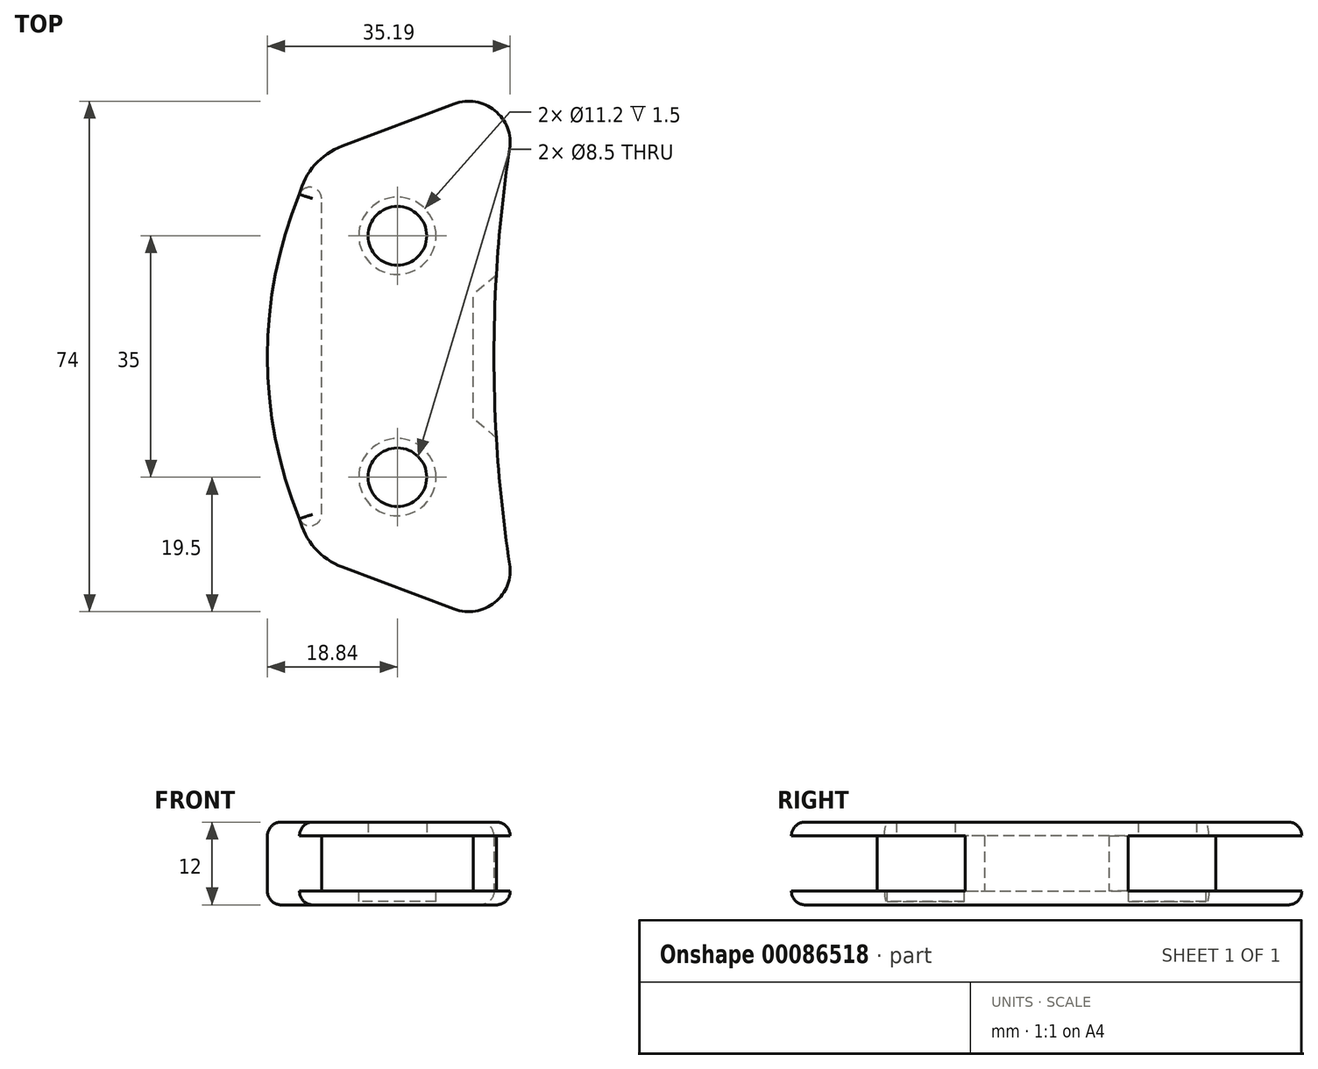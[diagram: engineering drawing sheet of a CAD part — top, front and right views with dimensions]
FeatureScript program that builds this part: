
annotation { "Feature Type Name" : "Feature", "Feature Type Description" : "" }
export const myFeature = defineFeature(function(context is Context, id is Id, definition is map)
    precondition{}
    {
        {
            var Q0;
            Q0=qCreatedBy(makeId("Top.planeOp"),FACE);
            var sketch = newSketch(context, id + "F0", { "sketchPlane" : qUnion([Q0])});
            skCircle(sketch, "E0", {"center": v(0, 17.5) * mm, "radius": 5.6 * mm, "construction": true});
            skCircle(sketch, "E1", {"center": v(0, -17.5) * mm, "radius": 5.6 * mm, "construction": true});
            skLineSegment(sketch, "E2", {"start": v(0, 17.5) * mm, "end": v(0, -17.5) * mm, "construction": true});
            skArc(sketch, "E3", {"start": v(15, 17.5) * mm, "mid": v(0, 32.5) * mm, "end": v(-15, 17.5) * mm, "construction": true});
            skArc(sketch, "E4", {"start": v(-15, -17.5) * mm, "mid": v(0, -32.5) * mm, "end": v(15, -17.5) * mm, "construction": true});
            skLineSegment(sketch, "E5", {"start": v(-15, 17.5) * mm, "end": v(-15, -17.5) * mm, "construction": true});
            skLineSegment(sketch, "E6", {"start": v(15, 17.5) * mm, "end": v(15, -17.5) * mm, "construction": true});
            skArc(sketch, "E7.0", {"start": v(18, 17.5) * mm, "mid": v(0, 35.5) * mm, "end": v(-18, 17.5) * mm, "construction": true});
            skLineSegment(sketch, "E7.1", {"start": v(18, 17.5) * mm, "end": v(18, -17.5) * mm, "construction": true});
            skArc(sketch, "E7.2", {"start": v(-18, -17.5) * mm, "mid": v(0, -35.5) * mm, "end": v(18, -17.5) * mm, "construction": true});
            skLineSegment(sketch, "E7.3", {"start": v(-18, 17.5) * mm, "end": v(-18, -17.5) * mm, "construction": true});
            skLineSegment(sketch, "E8", {"start": v(-8, 30.52) * mm, "end": v(8.24, 36.62) * mm});
            skLineSegment(sketch, "E9", {"start": v(-8, -30.52) * mm, "end": v(8.24, -36.62) * mm});
            skArc(sketch, "E10", {"start": v(-14.2, 23.51) * mm, "mid": v(-17, 0) * mm, "end": v(-14.2, -23.51) * mm});
            skArc(sketch, "E11", {"start": v(16.28, 30.1) * mm, "mid": v(14, 0) * mm, "end": v(16.28, -30.1) * mm});
            skArc(sketch, "E12", {"start": v(8.24, 36.62) * mm, "mid": v(14.12, 35.66) * mm, "end": v(16.28, 30.1) * mm});
            skArc(sketch, "E13", {"start": v(8.24, -36.62) * mm, "mid": v(14.12, -35.66) * mm, "end": v(16.28, -30.1) * mm});
            skLineSegment(sketch, "E14", {"start": v(0, 0) * mm, "end": v(83, 0) * mm, "construction": true});
            skLineSegment(sketch, "E15", {"start": v(10.35, 31) * mm, "end": v(10.35, -31) * mm, "construction": true});
            skPoint(sketch, "E16.visualSharp", {"position": v(-12.79, 28.72) * mm});
            skArc(sketch, "E16.filletArc", {"start": v(-8, 30.52) * mm, "mid": v(-11.97, 27.79) * mm, "end": v(-14.2, 23.51) * mm});
            skPoint(sketch, "E17.visualSharp", {"position": v(-12.79, -28.72) * mm});
            skArc(sketch, "E17.filletArc", {"start": v(-14.2, -23.51) * mm, "mid": v(-11.97, -27.79) * mm, "end": v(-8, -30.52) * mm});
            skSolve(sketch);
        }
        {
            var Q0;
            Q0=makeQuery(id+"F0.imprint","IMPRINT",FACE,{"disambiguationData":[TD([[makeQuery(id+"F0.imprint","IMPRINT",EDGE,{"derivedFrom":sQuery(id+"F0.wireOp",EDGE,"E8")}),-1.0]])]});
            extrude(context, id + "F1", {"entities" : qUnion([Q0]), "depth" : 2 * mm});
        }
        {
            var Q0;
            Q0=makeQuery(id+"F1.opExtrude","CAP_FACE",FACE,{"disambiguationData":[OSD([sQuery(id+"F0.wireOp",EDGE,"E8"),sQuery(id+"F0.wireOp",EDGE,"E9"),sQuery(id+"F0.wireOp",EDGE,"E10"),sQuery(id+"F0.wireOp",EDGE,"E11"),sQuery(id+"F0.wireOp",EDGE,"E12"),sQuery(id+"F0.wireOp",EDGE,"E13"),sQuery(id+"F0.wireOp",EDGE,"E16.filletArc"),sQuery(id+"F0.wireOp",EDGE,"E17.filletArc")])],"isStart":false});
            var sketch = newSketch(context, id + "F2", { "sketchPlane" : qUnion([Q0])});
            skCircle(sketch, "E18", {"center": v(0, 17.5) * mm, "radius": 5.6 * mm});
            skCircle(sketch, "E19", {"center": v(0, -17.5) * mm, "radius": 5.6 * mm});
            skLineSegment(sketch, "E20", {"start": v(0, 17.5) * mm, "end": v(0, -17.5) * mm, "construction": true});
            skArc(sketch, "E21", {"start": v(11, 17.5) * mm, "mid": v(0, 28.5) * mm, "end": v(-11, 17.5) * mm, "construction": true});
            skArc(sketch, "E22", {"start": v(-11, -17.5) * mm, "mid": v(0, -28.5) * mm, "end": v(11, -17.5) * mm, "construction": true});
            skLineSegment(sketch, "E23", {"start": v(-11, 17.5) * mm, "end": v(-11, -17.5) * mm, "construction": true});
            skLineSegment(sketch, "E24", {"start": v(11, 17.5) * mm, "end": v(11, -17.5) * mm, "construction": true});
            skArc(sketch, "E25.0", {"start": v(14, 17.5) * mm, "mid": v(0, 31.5) * mm, "end": v(-14, 17.5) * mm, "construction": true});
            skLineSegment(sketch, "E25.1", {"start": v(14, 17.5) * mm, "end": v(14, -17.5) * mm, "construction": true});
            skArc(sketch, "E25.2", {"start": v(-14, -17.5) * mm, "mid": v(0, -31.5) * mm, "end": v(14, -17.5) * mm, "construction": true});
            skLineSegment(sketch, "E25.3", {"start": v(-14, 17.5) * mm, "end": v(-14, -17.5) * mm, "construction": true});
            skLineSegment(sketch, "E26", {"start": v(-7.8, 25.97) * mm, "end": v(13.49, 36.11) * mm});
            skLineSegment(sketch, "E27", {"start": v(-7.8, -25.97) * mm, "end": v(13.49, -36.11) * mm});
            skArc(sketch, "E28", {"start": v(-10.24, 23.4) * mm, "mid": v(-15, 0) * mm, "end": v(-10.24, -23.4) * mm});
            skArc(sketch, "E29", {"start": v(19, 31.25) * mm, "mid": v(14, 0) * mm, "end": v(19, -31.25) * mm});
            skArc(sketch, "E30", {"start": v(13.49, 36.11) * mm, "mid": v(17.85, 35.5) * mm, "end": v(19, 31.25) * mm});
            skArc(sketch, "E31", {"start": v(13.49, -36.11) * mm, "mid": v(17.85, -35.5) * mm, "end": v(19, -31.25) * mm});
            skLineSegment(sketch, "E32", {"start": v(0, 0) * mm, "end": v(45, 0) * mm, "construction": true});
            skLineSegment(sketch, "E33", {"start": v(15.2, 32.5) * mm, "end": v(15.2, -32.5) * mm, "construction": true});
            skPoint(sketch, "E34.visualSharp", {"position": v(-9.46, 25.18) * mm});
            skArc(sketch, "E34.filletArc", {"start": v(-7.8, 25.97) * mm, "mid": v(-9.25, 24.92) * mm, "end": v(-10.24, 23.4) * mm});
            skPoint(sketch, "E35.visualSharp", {"position": v(-9.46, -25.18) * mm});
            skArc(sketch, "E35.filletArc", {"start": v(-10.24, -23.4) * mm, "mid": v(-9.25, -24.92) * mm, "end": v(-7.8, -25.97) * mm});
            skSolve(sketch);
        }
        {
            var Q0;
            Q0=makeQuery(id+"F2.imprint","IMPRINT",FACE,{"disambiguationData":[TD([[makeQuery(id+"F2.imprint","IMPRINT",EDGE,{"derivedFrom":sQuery(id+"F2.wireOp",EDGE,"E18")}),1.0]])]});
            var Q1;
            Q1=makeQuery(id+"F2.imprint","IMPRINT",FACE,{"disambiguationData":[TD([[makeQuery(id+"F2.imprint","IMPRINT",EDGE,{"derivedFrom":sQuery(id+"F2.wireOp",EDGE,"E19")}),1.0]])]});
            extrude(context, id + "F3", {"entities" : qUnion([Q0, Q1]), "operationType" : NewBodyOperationType.REMOVE, "oppositeDirection" : true, "depth" : 1.5 * mm});
        }
        {
            var Q0;
            Q0=qCreatedBy(makeId("Top.planeOp"),FACE);
            var sketch = newSketch(context, id + "F4", { "sketchPlane" : qUnion([Q0])});
            skCircle(sketch, "E36", {"center": v(0, 17.5) * mm, "radius": 5.6 * mm, "construction": true});
            skCircle(sketch, "E37", {"center": v(0, -17.5) * mm, "radius": 5.6 * mm, "construction": true});
            skLineSegment(sketch, "E38", {"start": v(0, 17.5) * mm, "end": v(0, -17.5) * mm, "construction": true});
            skArc(sketch, "E39", {"start": v(11, 17.5) * mm, "mid": v(0, 28.5) * mm, "end": v(-11, 17.5) * mm, "construction": true});
            skArc(sketch, "E40", {"start": v(-11, -17.5) * mm, "mid": v(0, -28.5) * mm, "end": v(11, -17.5) * mm, "construction": true});
            skLineSegment(sketch, "E41", {"start": v(-11, 22.88) * mm, "end": v(-11, -22.88) * mm});
            skLineSegment(sketch, "E42", {"start": v(11, 9) * mm, "end": v(11, -9) * mm});
            skArc(sketch, "E43.0", {"start": v(14, 17.5) * mm, "mid": v(0, 31.5) * mm, "end": v(-14, 17.5) * mm, "construction": true});
            skLineSegment(sketch, "E43.1", {"start": v(14, 17.5) * mm, "end": v(14, -17.5) * mm, "construction": true});
            skArc(sketch, "E43.2", {"start": v(-14, -17.5) * mm, "mid": v(0, -31.5) * mm, "end": v(14, -17.5) * mm, "construction": true});
            skLineSegment(sketch, "E43.3", {"start": v(-14, 17.5) * mm, "end": v(-14, -17.5) * mm, "construction": true});
            skArc(sketch, "E44", {"start": v(-14.2, 23.51) * mm, "mid": v(-18.84, 0) * mm, "end": v(-14.2, -23.51) * mm});
            skLineSegment(sketch, "E45", {"start": v(0, 0) * mm, "end": v(43, 0) * mm, "construction": true});
            skLineSegment(sketch, "E46", {"start": v(15.2, 32.5) * mm, "end": v(15.2, -32.5) * mm, "construction": true});
            skPoint(sketch, "E47.visualSharp", {"position": v(-13.13, 25.95) * mm});
            skPoint(sketch, "E48.visualSharp", {"position": v(-13.13, -25.95) * mm});
            skPoint(sketch, "E49.orphan", {"position": v(8.24, 36.62) * mm});
            skArc(sketch, "E50.0", {"start": v(14.35, 11.81) * mm, "mid": v(14, 0) * mm, "end": v(14.35, -11.81) * mm});
            skPoint(sketch, "E51.orphan", {"position": v(8.24, -36.62) * mm});
            skArc(sketch, "E52", {"start": v(-14.2, 23.51) * mm, "mid": v(-12.34, 24.5) * mm, "end": v(-11, 22.88) * mm});
            skArc(sketch, "E53.MirrorCS", {"start": v(-14.2, -23.51) * mm, "mid": v(-12.34, -24.5) * mm, "end": v(-11, -22.88) * mm});
            skLineSegment(sketch, "E54", {"start": v(11, 9) * mm, "end": v(14.35, 11.81) * mm});
            skLineSegment(sketch, "E55.MirrorCS", {"start": v(11, -9) * mm, "end": v(14.35, -11.81) * mm});
            skPoint(sketch, "E56.orphan", {"position": v(16.28, -30.1) * mm});
            skPoint(sketch, "E57.orphan", {"position": v(16.28, 30.1) * mm});
            skSolve(sketch);
        }
        {
            var Q0;
            Q0 = qSketchRegion(id + "F4", true);
            extrude(context, id + "F5", {"entities" : qUnion([Q0]), "operationType" : NewBodyOperationType.ADD, "depth" : 10 * mm});
        }
        {
            var Q0;
            Q0=makeQuery(id+"F5.opExtrude","CAP_FACE",FACE,{"disambiguationData":[OSD([sQuery(id+"F4.wireOp",EDGE,"E41"),sQuery(id+"F4.wireOp",EDGE,"E44"),sQuery(id+"F4.wireOp",EDGE,"5d6f1e88-396b-45d1-9be9-a47ba8d2432e"),sQuery(id+"F4.wireOp",EDGE,"66534eae-351e-46f8-825e-5522550ca6c2")])],"isStart":false});
            var sketch = newSketch(context, id + "F6", { "sketchPlane" : qUnion([Q0])});
            skLineSegment(sketch, "E58.0.0", {"start": v(-8, 30.52) * mm, "end": v(8.24, 36.62) * mm});
            skArc(sketch, "E58.0.1", {"start": v(8.24, 36.62) * mm, "mid": v(14.12, 35.66) * mm, "end": v(16.28, 30.1) * mm});
            skArc(sketch, "E58.0.2", {"start": v(16.28, 30.1) * mm, "mid": v(14, 0) * mm, "end": v(16.28, -30.1) * mm});
            skArc(sketch, "E58.0.3", {"start": v(16.28, -30.1) * mm, "mid": v(14.12, -35.66) * mm, "end": v(8.24, -36.62) * mm});
            skLineSegment(sketch, "E58.0.4", {"start": v(8.24, -36.62) * mm, "end": v(-8, -30.52) * mm});
            skArc(sketch, "E58.0.5", {"start": v(-8, -30.52) * mm, "mid": v(-11.97, -27.79) * mm, "end": v(-14.2, -23.51) * mm});
            skArc(sketch, "E58.0.7", {"start": v(-14.2, 23.51) * mm, "mid": v(-11.97, 27.79) * mm, "end": v(-8, 30.52) * mm});
            skArc(sketch, "E59.0", {"start": v(-14.2, 23.51) * mm, "mid": v(-18.84, 0) * mm, "end": v(-14.2, -23.51) * mm});
            skSolve(sketch);
        }
        {
            var Q0;
            Q0=makeQuery(id+"F6.imprint","IMPRINT",FACE,{"disambiguationData":[TD([[makeQuery(id+"F6.imprint","IMPRINT",EDGE,{"derivedFrom":sQuery(id+"F6.wireOp",EDGE,"E58.0.0")}),-1.0]])]});
            var Q1;
            Q1=makeQuery(id+"F6.imprint","IMPRINT",FACE,{"disambiguationData":[TD([[makeQuery(id+"F6.imprint","IMPRINT",EDGE,{"derivedFrom":makeQuery(id+"F5.opExtrude","CAP_EDGE",EDGE,{"disambiguationData":[OSD([sQuery(id+"F4.wireOp",EDGE,"E41")])],"isStart":false})}),-1.0]])]});
            extrude(context, id + "F7", {"entities" : qUnion([Q0, Q1]), "operationType" : NewBodyOperationType.ADD, "depth" : 2 * mm});
        }
        {
            var Q0;
            Q0=makeQuery(id+"F7.opExtrude","CAP_FACE",FACE,{"disambiguationData":[OSD([sQuery(id+"F6.wireOp",EDGE,"E58.0.0"),sQuery(id+"F6.wireOp",EDGE,"E58.0.1"),sQuery(id+"F6.wireOp",EDGE,"E58.0.2"),sQuery(id+"F6.wireOp",EDGE,"E58.0.3"),sQuery(id+"F6.wireOp",EDGE,"E58.0.4"),sQuery(id+"F6.wireOp",EDGE,"E58.0.5"),sQuery(id+"F6.wireOp",EDGE,"E58.0.7"),sQuery(id+"F6.wireOp",EDGE,"E59.0")])],"isStart":false});
            var Q1;
            Q1=makeQuery(id+"F5.opExtrude","CAP_EDGE",EDGE,{"disambiguationData":[OSD([sQuery(id+"F4.wireOp",EDGE,"E44")])],"isStart":true});
            var Q2;
            Q2=makeQuery(id+"F1.opExtrude","CAP_EDGE",EDGE,{"disambiguationData":[OSD([sQuery(id+"F0.wireOp",EDGE,"E11")])],"isStart":true});
            fillet(context, id + "F8", {"entities" : qUnion([Q0, Q1, Q2]), "radius" : 2 * mm, "tangentPropagation" : true, "allowEdgeOverflow" : false});
        }
        {
            var Q0;
            Q0=makeQuery(id+"F7.opExtrude","CAP_FACE",FACE,{"disambiguationData":[OSD([sQuery(id+"F6.wireOp",EDGE,"E58.0.0"),sQuery(id+"F6.wireOp",EDGE,"E58.0.1"),sQuery(id+"F6.wireOp",EDGE,"E58.0.2"),sQuery(id+"F6.wireOp",EDGE,"E58.0.3"),sQuery(id+"F6.wireOp",EDGE,"E58.0.4"),sQuery(id+"F6.wireOp",EDGE,"E58.0.5"),sQuery(id+"F6.wireOp",EDGE,"E58.0.7"),sQuery(id+"F6.wireOp",EDGE,"E59.0")])],"isStart":true});
            var sketch = newSketch(context, id + "F9", { "sketchPlane" : qUnion([Q0])});
            skCircle(sketch, "E60.0", {"center": v(0, -17.5) * mm, "radius": 5.6 * mm, "construction": true});
            skCircle(sketch, "E61.0", {"center": v(0, 17.5) * mm, "radius": 5.6 * mm, "construction": true});
            skCircle(sketch, "E62", {"center": v(0, 17.5) * mm, "radius": 4.25 * mm});
            skCircle(sketch, "E63", {"center": v(0, -17.5) * mm, "radius": 4.25 * mm});
            skSolve(sketch);
        }
        {
            var Q0;
            Q0 = qSketchRegion(id + "F9", true);
            extrude(context, id + "F10", {"entities" : qUnion([Q0]), "operationType" : NewBodyOperationType.REMOVE, "oppositeDirection" : true, "depth" : 2 * mm});
        }
    });
